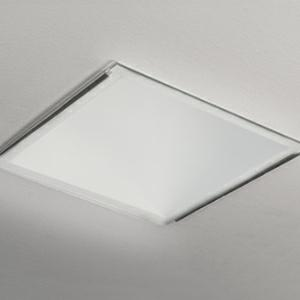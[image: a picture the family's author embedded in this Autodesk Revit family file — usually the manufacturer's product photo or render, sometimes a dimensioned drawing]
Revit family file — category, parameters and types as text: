
# Revit family: 3f_filippi_-_lucequadro_vs_3f_filippi_-_36578_-_lucequadro_led_3000_vs
name_source: partatom
category: Lighting Fixtures
units: mm (PartAtom-declared; Revit-internal decimal feet)

## family parameters
Cut with Voids When Loaded = No
Host = Face
Light Source = No
Part Type = Normal
Room Calculation Point = No
Round Connector Dimension = Use Diameter
Shared = No

## types (1)
- 3F Filippi - Lucequadro VS (1 x LED, 3076 lm, 28 W, 4000 K)
    Apparent Load = 28 VA
    Approval mark = ENEC
    CIE Flux Codes = 79 96 99 100 100
    Color Rendering = 80
    Color Temperature = 4000 K
    Control Gear = Electronic ballast
    Default Elevation = 1800 mm
    Description = ILLUMINOTECHNICAL
Luminous efficiency 100% (DLOR 100%, ULOR 0%).
Initial luminous flux of the luminaire 3076 lm.
Direct symmetric distribution.
Installation Interdistance Transv.D = 0.83 x hu - Long.D = 0.80 x hu.
Average luminance <3000 cd/m² for radial angles >65°.
Tabular UGR (CIE 117 - 4H-8H; S=0.25H; 70/50/20): RUG 18.2 - 18.
Beam angle: 58° - 57°.
Luminous efficacy 110 lm/W.
Lifetime (L90/B10): 30000 h. (tq+25°C)
Lifetime (L85/B10): 50000 h. (tq+25°C)
Lifetime (L70/B10): 80000 h. (tq+25°C)
Sudden decreased luminous flux after 50000 hours: 0% (C0).
Photobiological safety in compliance with IEC/TR 62778: RG1 low risk, (IEC 62471).
In compliance with IEC/EN 62722-2-1 - IEC/EN 62717 standards.

SOURCE
Compact LED module 3000/840.
Energy efficiency class (UE 2019/2020 - UE 2019/2015): D.
CIE 13.3 Colour rendering index: CRI >80 (R9 <50%).
IES TM-30 Fidelity Index: Rf = 84 Rg = 95.
CCT nominal colour temperature 4000 K.
Colour initial tolerance (MacAdam): SDCM 3.
Zhaga Book 3 compliant.

MECHANICAL
Housing in white painted steel.
Passive heat dissipator in anodised aluminium, oversized, for optimum thermal management of the LED module.
Flow recuperator in specular aluminium with superficial titanium-magnesium treatment, non-iridescent.
Moulded tempered anti-glare non-combustible glass, thickness 4 mm.
Lock-in mounting of the glass in the lateral seats in specular aluminium.
Fixing brackets in galvanised steel.
Slot-cover polycarbonate casings.
Dimensions: 235x235 mm, height 116 mm. Weight 2.135 kg.
IP44 protection degree for exposed part, IP20 for recessed part.
Mechanical strength to impacts IK08 (5 joule).
Glow-wire test resistance 960°C.

ELECTRICAL
Wiring on a separate unit.
Halogen Free electronic wiring 230V-50/60Hz, power factor 0.95, THD <25%, constant output current, SELV, class II, 1 driver.
Power of the luminaire 28 W.
CE - IEC 60598-1 - EN 60598-1.
SAFE FLICKER: PstLM=<1 and SVM=<0.4 (IEC TR 61547-1 and IEC TR 63158), to ensure a more comfortable and safe light.
Ambient temperature from 0°C to +25°C.
Temperature class T6 max 85°C.
Relative humidity UR: <85%.

INSTALLATION
Pull-up recessed fitting.
False ceiling carving: 210x210 mm.
All accessories dedicated to this product are available on the Catalog and on our website www.3F-Filippi.com.

ACCESSORIES
A0189 - Pair of reinforcing brackets for mineral fibre, metal and plasterboard panels, height 20 mm.

APPLICATIONS
Transit areas, corridors, commercial environments, display areas, shops and shop windows.

WARNING
Luminaire designed for disposal/recycling at end-of-life.
Replaceable (LED only) light source by a professional. Replaceable control gear by a professional.
    Height = 0 mm  [stored 0 ft]
    Lamp = 1 x LED
    Lamp Light Flux = 3076 lm
    Lamp Power = 28 W
    Lamp count = 1
    Length = 235 mm
    Lifetime = 50000 h
    Luminous efficacy = 110 lm/W
    Manufacturer = 3F Filippi
    ModVariant = No
    Model = 3F Filippi - 36578 - Lucequadro LED 3000 VS
    Mounting Place = Ceiling
    Mounting Type = Recessed
    Number of Poles = 1
    OnlyDefault = Yes
    Power Factor = 1
    Product Name = 3F Filippi - Lucequadro VS
    Product group = recessed luminaire
    ProductGroupID = 4
    Protection Class = Protection class II
    Protection Degree = IP 20
    RLX_Detail_Level = 1
    RLX_Emergency_Light_Flux = 0 lm
    RLX_Emergency_Type = 0
    RLX_Emergency_Type_DB = No
    RlxData = <blob elided: 57113 chars, md5=f3f1d496>
    Socket = socket
    Standby Power = 0 W
    System Light Flux = 3076 lm
    System Power = 28 W
    Type Comments = Product without accessories
    Type Image = 3ffilippi_36578.jpg
    URL = http://relux.com
    VarID = ---
    Voltage = 0 V
    Weight = 0.00 kg
    Width = 235 mm

note: [stored X ft] marks values corroborated as IEEE doubles in the binary element streams (Revit-internal decimal feet)

## geometry (parser evidence)
native form markers: Blend x4, Sweep x10
no freeform markers — native parametric forms only
